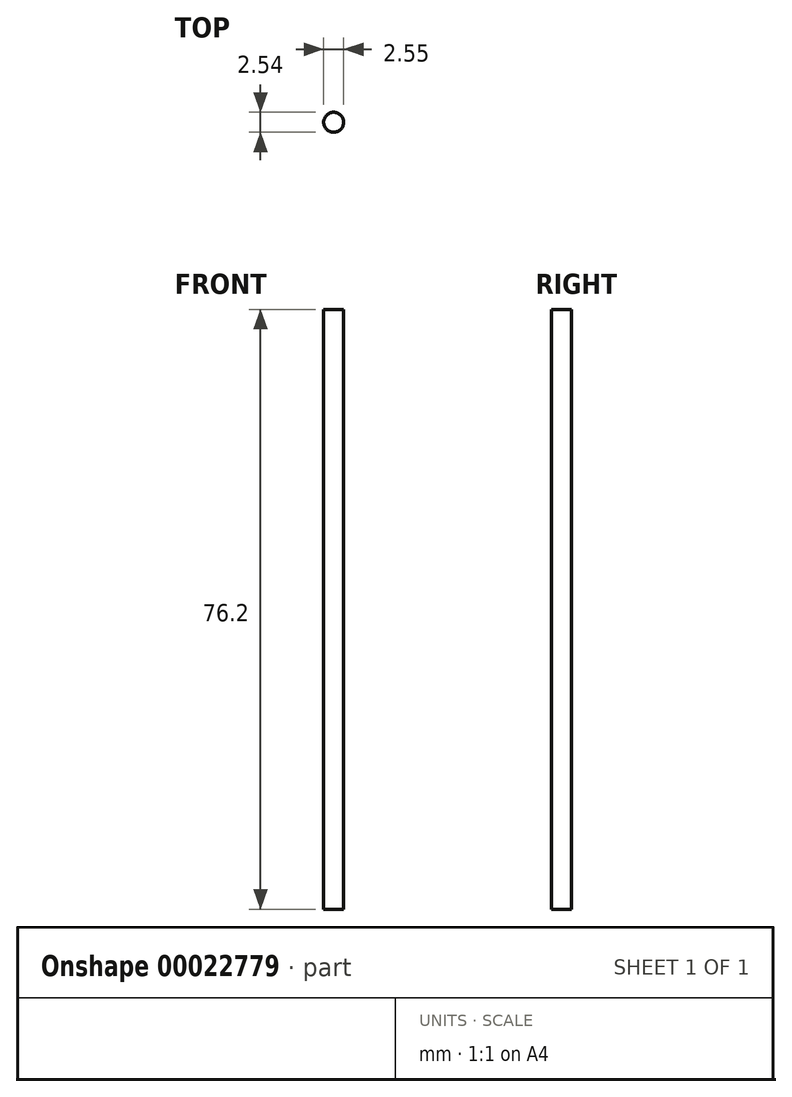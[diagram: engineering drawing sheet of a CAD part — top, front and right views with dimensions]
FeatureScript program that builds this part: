
annotation { "Feature Type Name" : "Feature", "Feature Type Description" : "" }
export const myFeature = defineFeature(function(context is Context, id is Id, definition is map)
    precondition{}
    {
        {
            var Q0;
            Q0=qCreatedBy(makeId("Front.planeOp"),FACE);
            var sketch = newSketch(context, id + "F0", { "sketchPlane" : qUnion([Q0])});
            skLineSegment(sketch, "E0.bottom", {"start": v(-0.63, 38.1) * mm, "end": v(0.63, 38.1) * mm});
            skLineSegment(sketch, "E0.top", {"start": v(-0.63, -38.1) * mm, "end": v(0.64, -38.1) * mm});
            skLineSegment(sketch, "E0.left", {"start": v(-0.63, 38.1) * mm, "end": v(-0.63, -38.1) * mm});
            skLineSegment(sketch, "E0.right", {"start": v(0.63, 38.1) * mm, "end": v(0.64, -38.1) * mm});
            skSolve(sketch);
        }
        {
            var Q0;
            Q0=makeQuery(id+"F0.imprint","IMPRINT",FACE,{"disambiguationData":[TD([[makeQuery(id+"F0.imprint","IMPRINT",EDGE,{"derivedFrom":sQuery(id+"F0.wireOp",EDGE,"E0.bottom")}),-1.0]])]});
            var Q1;
            Q1=sQuery(id+"F0.wireOp",EDGE,"E0.left");
            revolve(context, id + "F1", {"entities" : qUnion([Q0]), "axis" : qUnion([Q1]), "revolveType" : RevolveType.FULL});
        }
    });
